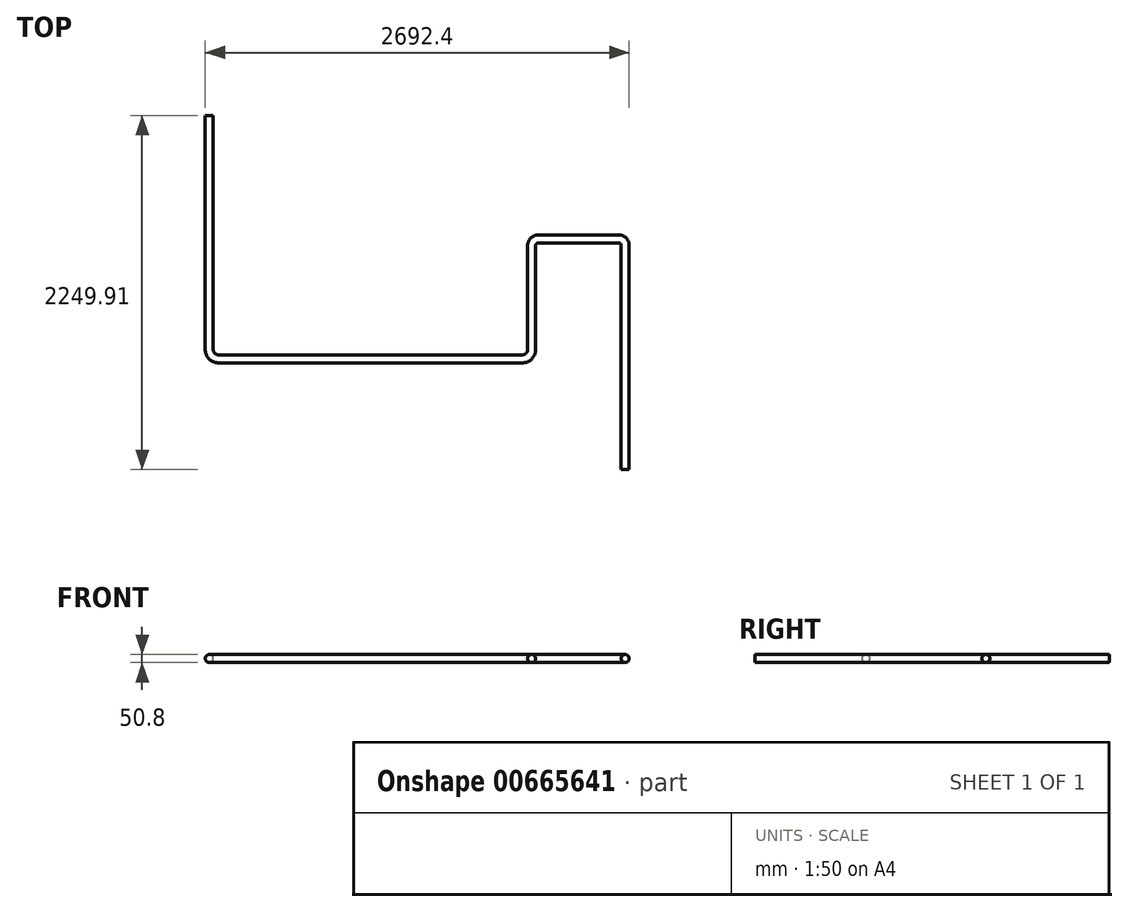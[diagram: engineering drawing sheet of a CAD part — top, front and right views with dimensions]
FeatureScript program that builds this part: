
annotation { "Feature Type Name" : "Feature", "Feature Type Description" : "" }
export const myFeature = defineFeature(function(context is Context, id is Id, definition is map)
    precondition{}
    {
        {
            var Q0;
            Q0=qCreatedBy(makeId("Top.planeOp"),FACE);
            var sketch = newSketch(context, id + "F0", { "sketchPlane" : qUnion([Q0])});
            skLineSegment(sketch, "E0", {"start": v(-50.8, 0) * mm, "end": v(-1981.2, 0) * mm});
            skLineSegment(sketch, "E1", {"start": v(-2032, 50.8) * mm, "end": v(-2032, 1538.71) * mm});
            skLineSegment(sketch, "E2", {"start": v(0, 50.8) * mm, "end": v(0, 711.2) * mm});
            skLineSegment(sketch, "E3", {"start": v(50.8, 762) * mm, "end": v(558.8, 762) * mm});
            skLineSegment(sketch, "E4", {"start": v(609.6, 711.2) * mm, "end": v(609.6, -711.2) * mm});
            skPoint(sketch, "E5.visualSharp", {"position": v(-2032, 0) * mm});
            skArc(sketch, "E5.filletArc", {"start": v(-2032, 50.8) * mm, "mid": v(-2017.12, 14.88) * mm, "end": v(-1981.2, 0) * mm});
            skPoint(sketch, "E6.visualSharp", {"position": v(0, 0) * mm});
            skArc(sketch, "E6.filletArc", {"start": v(-50.8, 0) * mm, "mid": v(-14.88, 14.88) * mm, "end": v(0, 50.8) * mm});
            skPoint(sketch, "E7.visualSharp", {"position": v(609.6, 762) * mm});
            skPoint(sketch, "E8.visualSharp", {"position": v(0, 762) * mm});
            skArc(sketch, "E8.filletArc", {"start": v(50.8, 762) * mm, "mid": v(14.88, 747.12) * mm, "end": v(0, 711.2) * mm});
            skArc(sketch, "E9.filletArc", {"start": v(609.6, 711.2) * mm, "mid": v(594.72, 747.12) * mm, "end": v(558.8, 762) * mm});
            skPoint(sketch, "E10", {"position": v(-1558.5, 0) * mm});
            skPoint(sketch, "E11", {"position": v(-542.5, 0) * mm});
            skPoint(sketch, "E12", {"position": v(-2032, 1192.45) * mm});
            skPoint(sketch, "E13", {"position": v(-2032, 390.88) * mm});
            skSolve(sketch);
        }
        {
            var Q0;
            Q0=sQuery(id+"F0.wireOp",VERTEX,"E4.end");
            var Q1;
            Q1=sQuery(id+"F0.wireOp",EDGE,"E4");
            cPlane(context, id + "F1", {"entities" : qUnion([Q0, Q1]), "cplaneType" : CPlaneType.LINE_POINT, "offset" : 25.4 * mm, "width" : 152.4 * mm, "height" : 152.4 * mm});
        }
        {
            var Q0;
            Q0=qCreatedBy(id+"F1.planeOp",FACE);
            var sketch = newSketch(context, id + "F2", { "sketchPlane" : qUnion([Q0])});
            skCircle(sketch, "E14", {"center": v(601.86, 0) * mm, "radius": 25.4 * mm});
            skSolve(sketch);
        }
        {
            var Q0;
            Q0=makeQuery(id+"F2.imprint","IMPRINT",FACE,{"disambiguationData":[TD([[makeQuery(id+"F2.imprint","IMPRINT",EDGE,{"derivedFrom":sQuery(id+"F2.wireOp",EDGE,"E14")}),1.0]])]});
            var Q1;
            Q1 = qConstructionFilter(qBodyType(qCreatedBy(id + "F0" ,EDGE), BodyType.WIRE), ConstructionObject.NO);
            sweep(context, id + "F3", {"profiles" : qUnion([Q0]), "path" : qUnion([Q1])});
        }
    });
